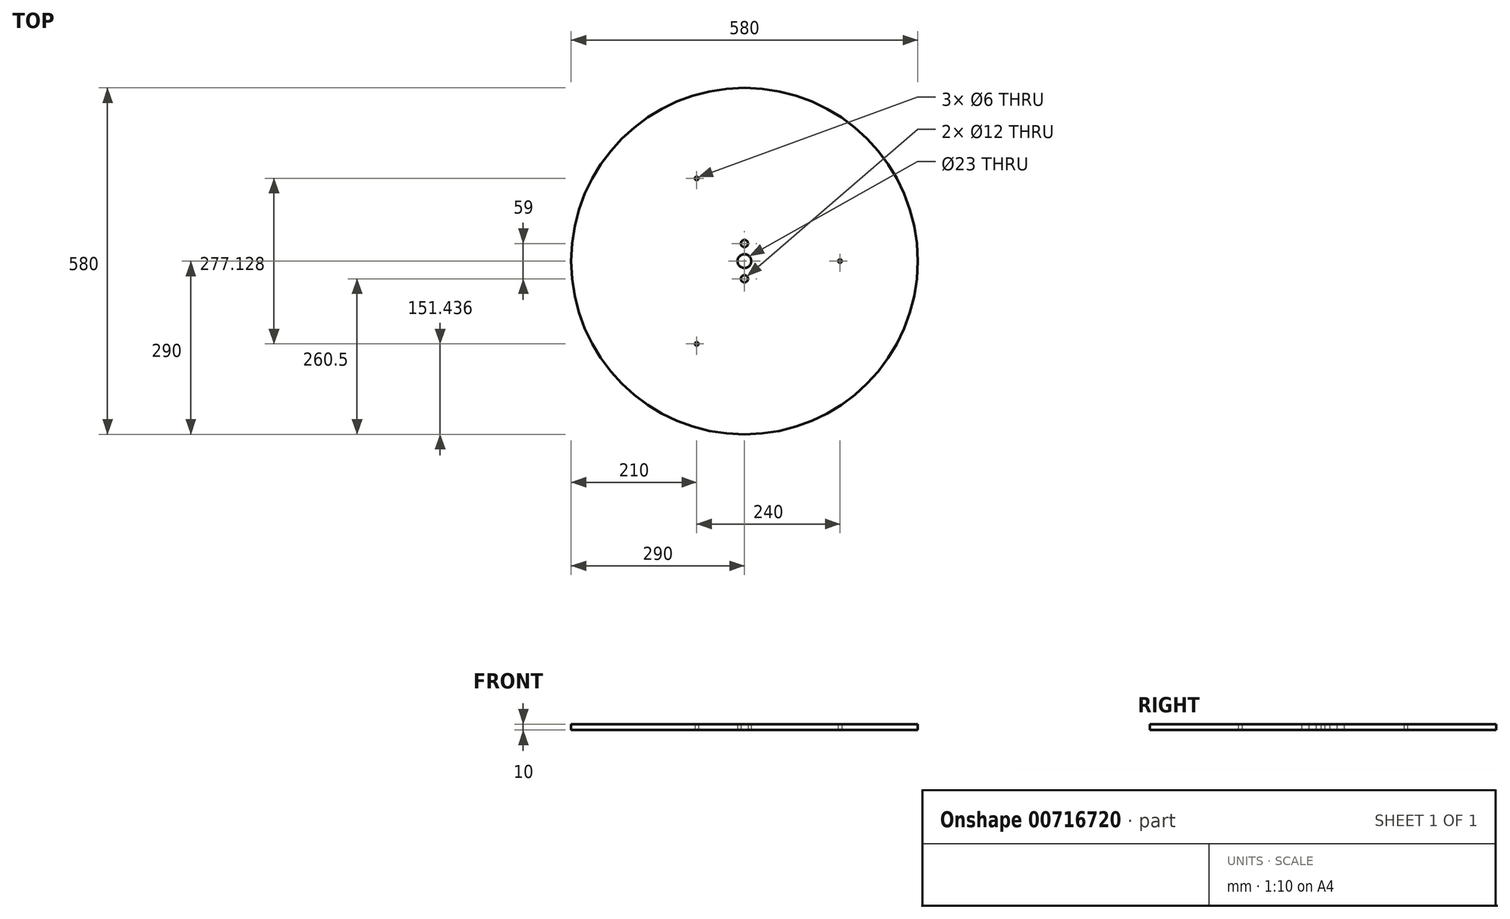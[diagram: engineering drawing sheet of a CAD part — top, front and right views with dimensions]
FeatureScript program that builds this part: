
annotation { "Feature Type Name" : "Feature", "Feature Type Description" : "" }
export const myFeature = defineFeature(function(context is Context, id is Id, definition is map)
    precondition{}
    {
        {
            var Q0;
            Q0=qCreatedBy(makeId("Top.planeOp"),FACE);
            var sketch = newSketch(context, id + "F0", { "sketchPlane" : qUnion([Q0])});
            skCircle(sketch, "E0", {"center": v(0, 0) * mm, "radius": 290 * mm});
            skCircle(sketch, "E1", {"center": v(0, 0) * mm, "radius": 11.5 * mm});
            skCircle(sketch, "E2", {"center": v(0, 29.5) * mm, "radius": 6 * mm});
            skCircle(sketch, "E3", {"center": v(0, -29.5) * mm, "radius": 6 * mm});
            skCircle(sketch, "E4", {"center": v(160, 0) * mm, "radius": 3 * mm});
            skCircle(sketch, "E5.1.0", {"center": v(-80, 138.56) * mm, "radius": 3 * mm});
            skCircle(sketch, "E5.2.0", {"center": v(-80, -138.56) * mm, "radius": 3 * mm});
            skSolve(sketch);
        }
        {
            var Q0;
            Q0=makeQuery(id+"F0.imprint","IMPRINT",FACE,{"disambiguationData":[TD([[makeQuery(id+"F0.imprint","IMPRINT",EDGE,{"derivedFrom":sQuery(id+"F0.wireOp",EDGE,"E0")}),1.0]])]});
            extrude(context, id + "F1", {"entities" : qUnion([Q0]), "depth" : 10 * mm, "offsetDistance" : 25 * mm});
        }
    });
